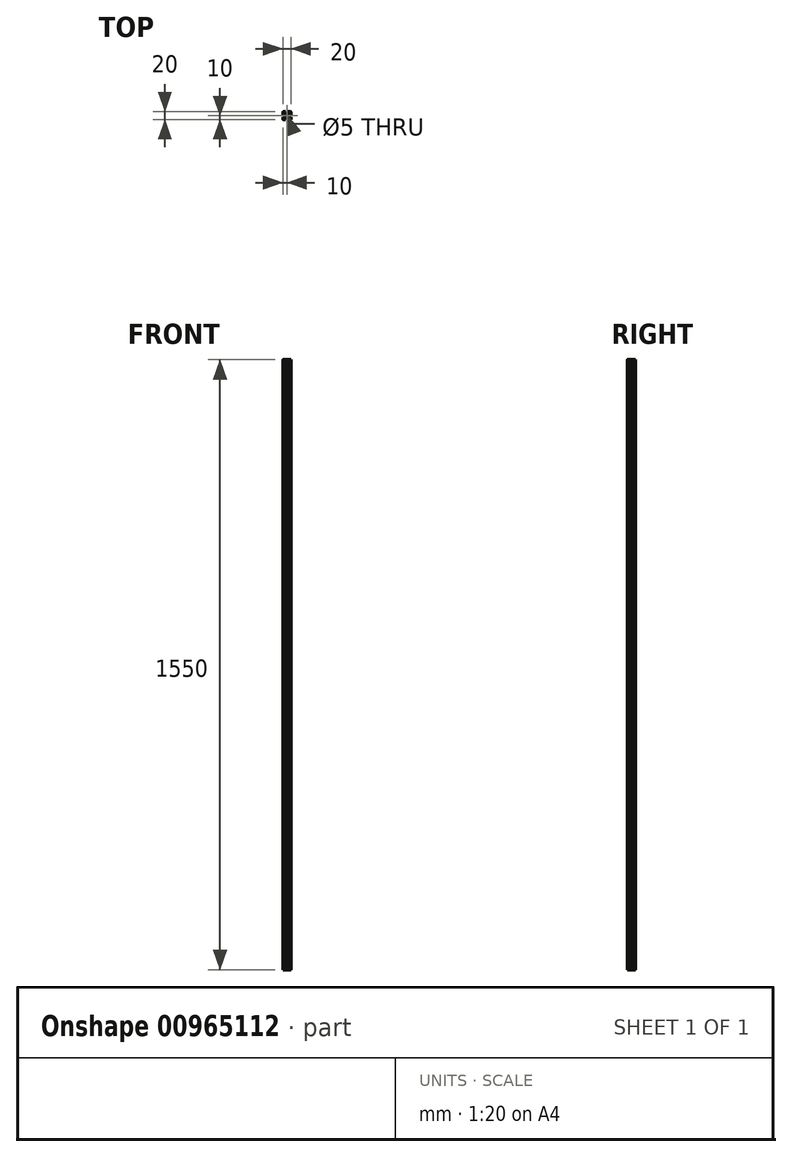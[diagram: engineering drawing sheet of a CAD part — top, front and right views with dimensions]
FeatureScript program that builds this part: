
annotation { "Feature Type Name" : "Feature", "Feature Type Description" : "" }
export const myFeature = defineFeature(function(context is Context, id is Id, definition is map)
    precondition{}
    {
        {
            var Q0;
            Q0=qCreatedBy(makeId("Top.planeOp"),FACE);
            var sketch = newSketch(context, id + "F0", { "sketchPlane" : qUnion([Q0])});
            skCircle(sketch, "E0", {"center": v(10, 10) * mm, "radius": 2.5 * mm});
            skLineSegment(sketch, "E1", {"start": v(0, 0) * mm, "end": v(10, 10) * mm, "construction": true});
            skLineSegment(sketch, "E2", {"start": v(1.4, 2.39) * mm, "end": v(1.4, 6.8) * mm});
            skLineSegment(sketch, "E3", {"start": v(1.4, 6.8) * mm, "end": v(0, 6.8) * mm});
            skLineSegment(sketch, "E4", {"start": v(0, 6.8) * mm, "end": v(0, 0) * mm});
            skLineSegment(sketch, "E5", {"start": v(7.49, 6.5) * mm, "end": v(2.39, 1.4) * mm});
            skLineSegment(sketch, "E6", {"start": v(2.39, 1.4) * mm, "end": v(6.8, 1.4) * mm});
            skLineSegment(sketch, "E7", {"start": v(6.8, 1.4) * mm, "end": v(6.8, 0) * mm});
            skLineSegment(sketch, "E8", {"start": v(6.8, 0) * mm, "end": v(0, 0) * mm});
            skLineSegment(sketch, "E9", {"start": v(10, 10) * mm, "end": v(20, 20) * mm, "construction": true});
            skLineSegment(sketch, "E10", {"start": v(10, 10) * mm, "end": v(0, 20) * mm, "construction": true});
            skLineSegment(sketch, "E11", {"start": v(10, 10) * mm, "end": v(20, 0) * mm, "construction": true});
            skLineSegment(sketch, "E12", {"start": v(1.4, 17.61) * mm, "end": v(6.5, 12.51) * mm});
            skLineSegment(sketch, "E13", {"start": v(1.4, 17.61) * mm, "end": v(1.4, 13.2) * mm});
            skLineSegment(sketch, "E14", {"start": v(1.4, 13.2) * mm, "end": v(0, 13.2) * mm});
            skLineSegment(sketch, "E15", {"start": v(0, 13.2) * mm, "end": v(0, 20) * mm});
            skLineSegment(sketch, "E16", {"start": v(7.49, 13.5) * mm, "end": v(2.39, 18.6) * mm});
            skLineSegment(sketch, "E17", {"start": v(2.39, 18.6) * mm, "end": v(6.8, 18.6) * mm});
            skLineSegment(sketch, "E18", {"start": v(6.8, 18.6) * mm, "end": v(6.8, 20) * mm});
            skLineSegment(sketch, "E19", {"start": v(6.8, 20) * mm, "end": v(0, 20) * mm});
            skLineSegment(sketch, "E20", {"start": v(12.51, 13.5) * mm, "end": v(17.61, 18.6) * mm});
            skLineSegment(sketch, "E21", {"start": v(17.61, 18.6) * mm, "end": v(13.2, 18.6) * mm});
            skLineSegment(sketch, "E22", {"start": v(13.2, 18.6) * mm, "end": v(13.2, 20) * mm});
            skLineSegment(sketch, "E23", {"start": v(13.2, 20) * mm, "end": v(20, 20) * mm});
            skLineSegment(sketch, "E24", {"start": v(13.5, 12.51) * mm, "end": v(18.6, 17.61) * mm});
            skLineSegment(sketch, "E25", {"start": v(18.6, 17.61) * mm, "end": v(18.6, 13.2) * mm});
            skLineSegment(sketch, "E26", {"start": v(18.6, 13.2) * mm, "end": v(20, 13.2) * mm});
            skLineSegment(sketch, "E27", {"start": v(20, 13.2) * mm, "end": v(20, 20) * mm});
            skLineSegment(sketch, "E28", {"start": v(18.6, 2.39) * mm, "end": v(18.6, 6.8) * mm});
            skLineSegment(sketch, "E29", {"start": v(18.6, 6.8) * mm, "end": v(20, 6.8) * mm});
            skLineSegment(sketch, "E30", {"start": v(20, 6.8) * mm, "end": v(20, 0) * mm});
            skLineSegment(sketch, "E31", {"start": v(12.51, 6.5) * mm, "end": v(17.61, 1.4) * mm});
            skLineSegment(sketch, "E32", {"start": v(17.61, 1.4) * mm, "end": v(13.2, 1.4) * mm});
            skLineSegment(sketch, "E33", {"start": v(13.2, 1.4) * mm, "end": v(13.2, 0) * mm});
            skLineSegment(sketch, "E34", {"start": v(13.2, 0) * mm, "end": v(20, 0) * mm});
            skLineSegment(sketch, "E35", {"start": v(12.51, 6.5) * mm, "end": v(7.49, 6.5) * mm});
            skLineSegment(sketch, "E36", {"start": v(7.49, 13.5) * mm, "end": v(12.51, 13.5) * mm});
            skLineSegment(sketch, "E37", {"start": v(10, 10) * mm, "end": v(10, 0) * mm, "construction": true});
            skLineSegment(sketch, "E38", {"start": v(10, 10) * mm, "end": v(18.77, 10) * mm, "construction": true});
            skLineSegment(sketch, "E39", {"start": v(10, 10) * mm, "end": v(10, 20.74) * mm, "construction": true});
            skLineSegment(sketch, "E40", {"start": v(10, 10) * mm, "end": v(0, 10) * mm, "construction": true});
            skLineSegment(sketch, "E41.bottom", {"start": v(0, 0) * mm, "end": v(20, 0) * mm, "construction": true});
            skLineSegment(sketch, "E41.top", {"start": v(0, 20) * mm, "end": v(20, 20) * mm, "construction": true});
            skLineSegment(sketch, "E41.left", {"start": v(0, 0) * mm, "end": v(0, 20) * mm, "construction": true});
            skLineSegment(sketch, "E41.right", {"start": v(20, 0) * mm, "end": v(20, 20) * mm, "construction": true});
            skLineSegment(sketch, "E42", {"start": v(18.6, 2.39) * mm, "end": v(13.5, 7.49) * mm});
            skLineSegment(sketch, "E43", {"start": v(13.5, 7.49) * mm, "end": v(13.5, 12.51) * mm});
            skLineSegment(sketch, "E44", {"start": v(1.4, 2.39) * mm, "end": v(6.5, 7.62) * mm});
            skLineSegment(sketch, "E45", {"start": v(6.5, 7.62) * mm, "end": v(6.5, 12.51) * mm});
            skSolve(sketch);
        }
        {
            var Q0;
            Q0=makeQuery(id+"F0.imprint","IMPRINT",FACE,{"disambiguationData":[TD([[makeQuery(id+"F0.imprint","IMPRINT",EDGE,{"derivedFrom":sQuery(id+"F0.wireOp",EDGE,"E0")}),-1.0]])]});
            extrude(context, id + "F1", {"entities" : qUnion([Q0]), "depth" : 1550 * mm, "offsetDistance" : 25 * mm});
        }
        {
            var Q0;
            Q0=makeQuery(id+"F1.opExtrude","SWEPT_EDGE",EDGE,{"disambiguationData":[OSD([sQuery(id+"F0.wireOp",EDGE,"E4"),sQuery(id+"F0.wireOp",EDGE,"E8")])]});
            var Q1;
            Q1=makeQuery(id+"F1.opExtrude","SWEPT_EDGE",EDGE,{"disambiguationData":[OSD([sQuery(id+"F0.wireOp",EDGE,"E15"),sQuery(id+"F0.wireOp",EDGE,"E19")])]});
            var Q2;
            Q2=makeQuery(id+"F1.opExtrude","SWEPT_EDGE",EDGE,{"disambiguationData":[OSD([sQuery(id+"F0.wireOp",EDGE,"E23"),sQuery(id+"F0.wireOp",EDGE,"E27")])]});
            var Q3;
            Q3=makeQuery(id+"F1.opExtrude","SWEPT_EDGE",EDGE,{"disambiguationData":[OSD([sQuery(id+"F0.wireOp",EDGE,"E30"),sQuery(id+"F0.wireOp",EDGE,"E34")])]});
            fillet(context, id + "F2", {"entities" : qUnion([Q0, Q1, Q2, Q3]), "tangentPropagation" : true, "radius" : 0.5 * mm, "defaultsChanged" : true, "vertexSettings" : [], "allowEdgeOverflow" : false});
        }
    });
